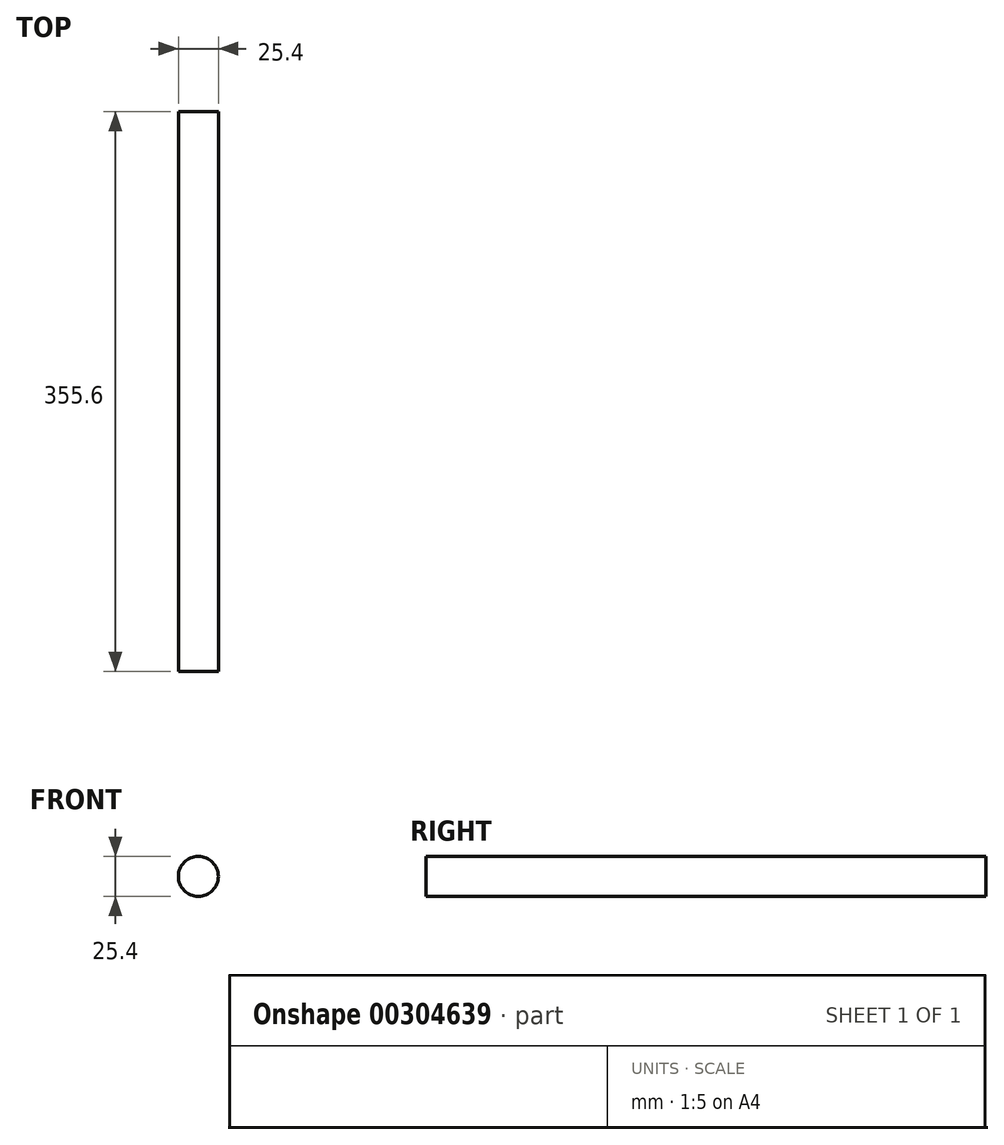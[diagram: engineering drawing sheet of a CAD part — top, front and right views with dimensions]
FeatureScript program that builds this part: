
annotation { "Feature Type Name" : "Feature", "Feature Type Description" : "" }
export const myFeature = defineFeature(function(context is Context, id is Id, definition is map)
    precondition{}
    {
        {
            var Q0;
            Q0=qCreatedBy(makeId("Front.planeOp"),FACE);
            var sketch = newSketch(context, id + "F0", { "sketchPlane" : qUnion([Q0])});
            skCircle(sketch, "E0", {"center": v(0, 0) * mm, "radius": 12.7 * mm});
            skSolve(sketch);
        }
        {
            var Q0;
            Q0 = qSketchRegion(id + "F0", true);
            extrude(context, id + "F1", {"entities" : qUnion([Q0]), "depth" : 355.6 * mm});
        }
    });
